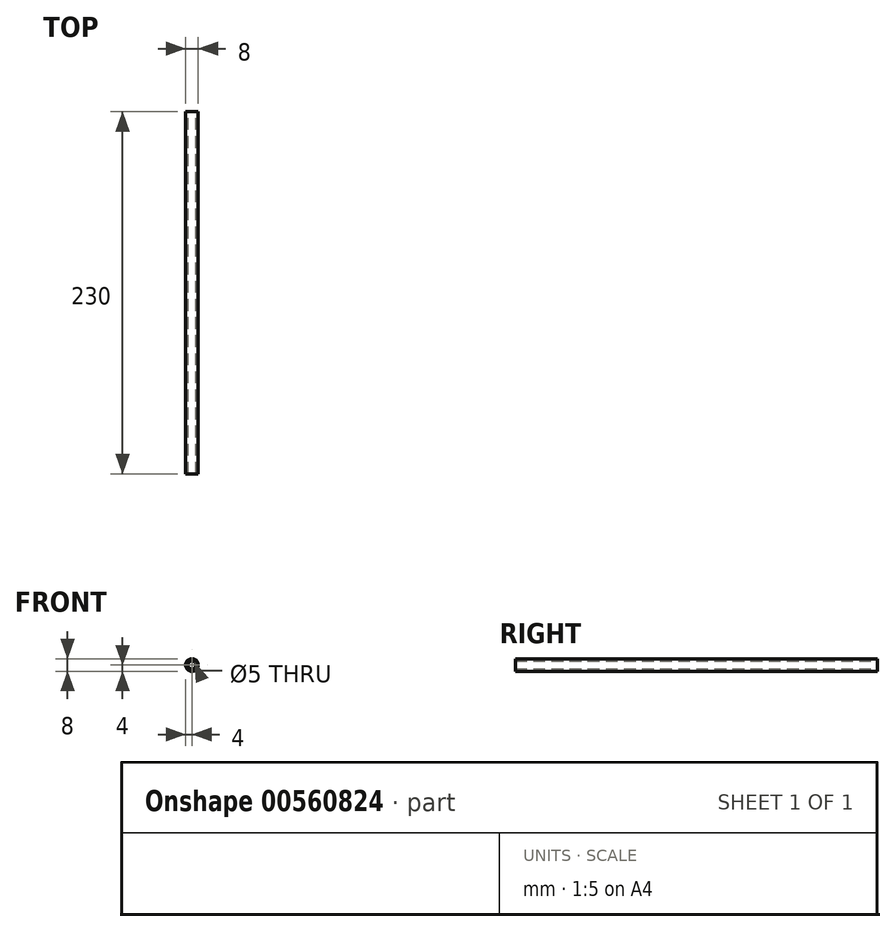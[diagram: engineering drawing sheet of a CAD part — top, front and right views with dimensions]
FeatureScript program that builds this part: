
annotation { "Feature Type Name" : "Feature", "Feature Type Description" : "" }
export const myFeature = defineFeature(function(context is Context, id is Id, definition is map)
    precondition{}
    {
        {
            var Q0;
            Q0=qCreatedBy(makeId("Front.planeOp"),FACE);
            var sketch = newSketch(context, id + "F0", { "sketchPlane" : qUnion([Q0])});
            skCircle(sketch, "E0", {"center": v(0, 0) * mm, "radius": 4 * mm});
            skCircle(sketch, "E1", {"center": v(0, 0) * mm, "radius": 2.5 * mm});
            skSolve(sketch);
        }
        {
            var Q0;
            Q0=qSketchRegion(id+"F0",true);
            extrude(context, id + "F1", {"entities" : qUnion([Q0]), "endBound" : BoundingType.SYMMETRIC, "depth" : 230 * mm, "offsetDistance" : 25 * mm});
        }
    });
